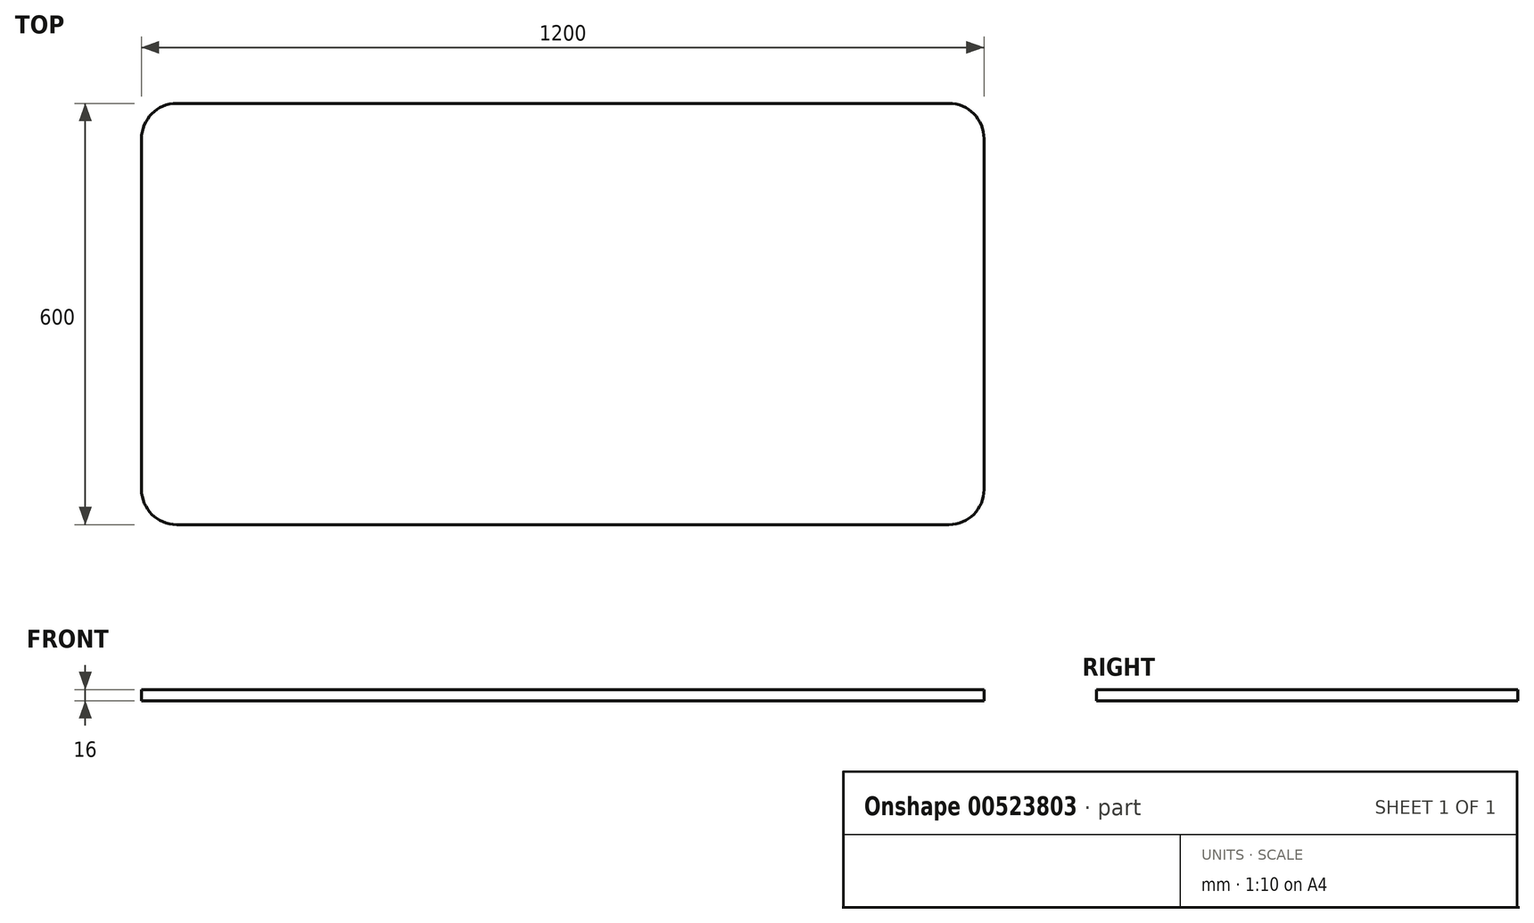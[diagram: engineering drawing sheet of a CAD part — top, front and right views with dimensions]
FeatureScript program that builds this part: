
annotation { "Feature Type Name" : "Feature", "Feature Type Description" : "" }
export const myFeature = defineFeature(function(context is Context, id is Id, definition is map)
    precondition{}
    {
        {
            var Q0;
            Q0=qCreatedBy(makeId("Top.planeOp"),FACE);
            var sketch = newSketch(context, id + "F0", { "sketchPlane" : qUnion([Q0])});
            skLineSegment(sketch, "E0.bottom", {"start": v(550, -300) * mm, "end": v(-550, -300) * mm});
            skLineSegment(sketch, "E0.top", {"start": v(550, 300) * mm, "end": v(-550, 300) * mm});
            skLineSegment(sketch, "E0.left", {"start": v(600, -250) * mm, "end": v(600, 250) * mm});
            skLineSegment(sketch, "E0.right", {"start": v(-600, -250) * mm, "end": v(-600, 250) * mm});
            skPoint(sketch, "E0.middle", {"position": v(0, 0) * mm});
            skPoint(sketch, "E1.visualSharp", {"position": v(-600, 300) * mm});
            skArc(sketch, "E1.filletArc", {"start": v(-550, 300) * mm, "mid": v(-585.36, 285.36) * mm, "end": v(-600, 250) * mm});
            skPoint(sketch, "E2.visualSharp", {"position": v(-600, -300) * mm});
            skArc(sketch, "E2.filletArc", {"start": v(-600, -250) * mm, "mid": v(-585.36, -285.36) * mm, "end": v(-550, -300) * mm});
            skPoint(sketch, "E3.visualSharp", {"position": v(600, -300) * mm});
            skArc(sketch, "E3.filletArc", {"start": v(550, -300) * mm, "mid": v(585.36, -285.36) * mm, "end": v(600, -250) * mm});
            skPoint(sketch, "E4.visualSharp", {"position": v(600, 300) * mm});
            skArc(sketch, "E4.filletArc", {"start": v(600, 250) * mm, "mid": v(585.36, 285.36) * mm, "end": v(550, 300) * mm});
            skSolve(sketch);
        }
        {
            var Q0;
            Q0=makeQuery(id+"F0.imprint","IMPRINT",FACE,{"disambiguationData":[TD([[makeQuery(id+"F0.imprint","IMPRINT",EDGE,{"derivedFrom":sQuery(id+"F0.wireOp",EDGE,"E0.bottom")}),-1.0]])]});
            extrude(context, id + "F1", {"entities" : qUnion([Q0]), "depth" : 16 * mm, "offsetDistance" : 25 * mm});
        }
    });
